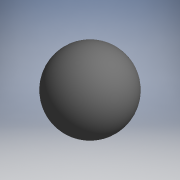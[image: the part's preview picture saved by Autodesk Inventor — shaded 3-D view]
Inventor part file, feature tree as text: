
AUTODESK INVENTOR PART (.ipt)
format: ipt  version: 2017.3 (Build 213256000, 256)  size: 111,104 bytes
history: native  units: mm (DEFAULTED — no unit token found)
features: other x7, revolve x1, sketch x1
ambient origin geometry x8: Origin, YZ Plane, XZ Plane, XY Plane, X Axis, Y Axis, Z Axis, Center Point
bodies: Solid1 (feature_tree)
feature tree (9):
  revolve  "Revolution1"  [1 undecoded]
  other  "ip_st_b_XY"
  other  "ip_st_b_YZ"
  other  "ip_st_b_ZX"
  other  "ip_st_b_X"
  other  "ip_st_b_Y"
  other  "ip_st_b_Z"
  other  "ip_st_b_Center"
  sketch  "Sketch_1"  dims[d0=360.0deg]
note: 1 required parameter value undecoded (feature->parameter linkage not recoverable at this tier; creation-order binding heuristic only, values carry confidence <= 0.55)
